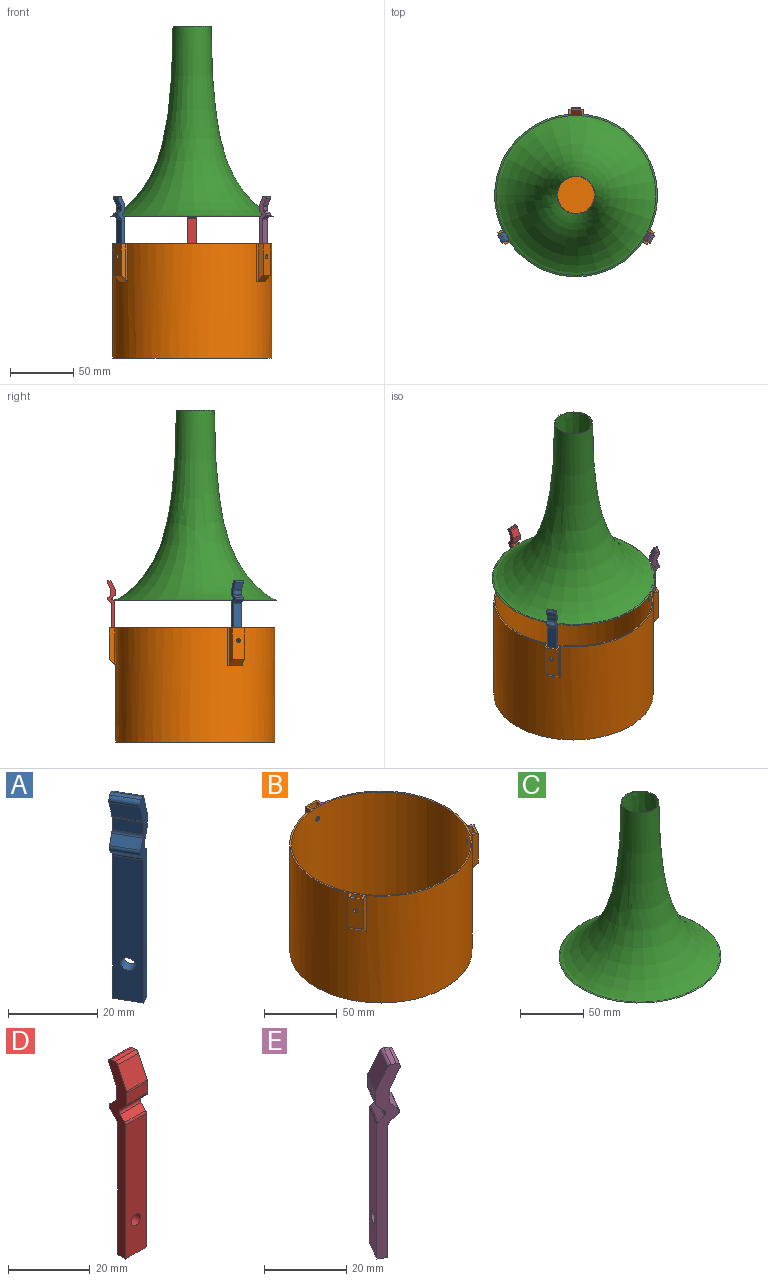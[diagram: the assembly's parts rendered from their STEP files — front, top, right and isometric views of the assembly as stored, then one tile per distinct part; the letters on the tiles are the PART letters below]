
ASSEMBLY  parts=5 mates=4
PART A: 25 faces, bbox 9.1x9.4x57.3 mm
  f0: plane 7.24x5.33mm, normal (-0.61,-0.35,0.71), area 20.4mm2, adj f12,f13,f15,f22
  f1: plane 6.24x3.6mm, normal (-0.87,-0.5,0), area 24.2mm2, adj f12,f13,f15,f16
  f2: plane 7.55x5.87mm, normal (-0.78,-0.45,-0.42), area 44.7mm2, adj f12,f13,f16,f23
  f3: plane 6.88x4.72mm, normal (0,0,1), area 9.3mm2, adj f12,f13,f23,f24
  f4: plane 7.74x6.47mm, normal (0.78,0.45,0.42), area 51.4mm2, adj f12,f13,f17,f24
  f5: plane 6.24x3.6mm, normal (0.87,0.5,0), area 24.2mm2, adj f12,f13,f17,f18
  f6: plane 7.24x5.33mm, normal (0.61,0.35,-0.71), area 20.4mm2, adj f12,f13,f18,f19
  f7: plane 7.04x4.99mm, normal (0.61,0.35,0.71), area 16.3mm2, adj f12,f13,f19,f20
  f8: plane 39.99x6.24mm, normal (0.87,0.5,0), area 278.8mm2, adj f9,f12,f13,f14,f20
  f9: plane 7.59x5.94mm, normal (0,0,-1), area 19.4mm2, adj f8,f10,f12,f13
  f10: plane 39.19x6.24mm, normal (-0.87,-0.5,0), area 273.1mm2, adj f9,f12,f13,f14,f21
  f11: plane 7.44x5.68mm, normal (-0.61,-0.35,-0.71), area 24.4mm2, adj f12,f13,f21,f22
  f12: plane 57.25x5.47mm, normal (-0.5,0.87,0), area 167.7mm2, adj f0,f1,f2,f3,f4,f5,f6,f7
  f13: plane 57.25x5.47mm, normal (0.5,-0.87,0), area 167.7mm2, adj f0,f1,f2,f3,f4,f5,f6,f7
  f14: cylinder r=1.7mm len=4.29mm, axis (-0.87,-0.5,0), area 28.8mm2, adj f8,f10
  f15: cylinder r=1mm len=6.38mm, axis (-0.5,0.87,0), area 5.7mm2, adj f0,f1,f12,f13
  f16: cylinder r=1mm len=6.28mm, axis (0.5,-0.87,0), area 3.1mm2, adj f1,f2,f12,f13
  f17: cylinder r=1mm len=6.28mm, axis (-0.5,0.87,0), area 3.1mm2, adj f4,f5,f12,f13
  f18: cylinder r=1mm len=6.38mm, axis (0.5,-0.87,0), area 5.7mm2, adj f5,f6,f12,f13
  f19: cylinder r=1mm len=6.38mm, axis (-0.5,0.87,0), area 11.3mm2, adj f6,f7,f12,f13
  f20: cylinder r=1mm len=6.38mm, axis (0.5,-0.87,0), area 5.7mm2, adj f7,f8,f12,f13
  f21: cylinder r=1mm len=6.38mm, axis (-0.5,0.87,0), area 5.7mm2, adj f10,f11,f12,f13
  f22: cylinder r=1mm len=6.38mm, axis (0.5,-0.87,0), area 11.3mm2, adj f0,f11,f12,f13
  f23: cylinder r=1mm len=6.74mm, axis (0.5,-0.87,0), area 14.5mm2, adj f2,f3,f12,f13
  f24: cylinder r=1mm len=6.69mm, axis (0.5,-0.87,0), area 8.2mm2, adj f3,f4,f12,f13
PART B: 47 faces, bbox 125.6x130.7x90 mm
  f0: cylinder r=61.6mm len=123.2mm, axis (0,0,-1), area 34497.3mm2, adj f1,f4,f16,f30,f44
  f1: plane 130.7x125.6mm, normal (0,0,1), area 560.2mm2, adj f0,f2,f5,f6,f7,f10,f11,f12
  f2: cylinder r=62.8mm len=125.6mm, axis (0,0,-1), area 34341.1mm2, adj f1,f3,f14,f17,f18,f28,f31,f32
  f3: plane 125.6x125.6mm, normal (0,0,-1), area 12389.9mm2, adj f2
  f4: plane 123.2x123.2mm, normal (0,0,1), area 11921mm2, adj f0
  f5: plane 29.11x4.45mm, normal (-1,0,0), area 119.5mm2, adj f1,f7,f8,f14,f18
  f6: plane 29.11x4.45mm, normal (1,0,0), area 119.5mm2, adj f1,f7,f8,f14,f17
  f7: plane 25x11.2mm, normal (0,1,0), area 270.9mm2, adj f1,f5,f6,f8,f15
  f8: plane 11.2x0.33mm, normal (0,0,-1), area 2mm2, adj f5,f6,f7,f14
  f9: plane 8x3.5mm, normal (0,0,1), area 28mm2, adj f10,f11,f12,f13
  f10: plane 24x8mm, normal (0,1,0), area 182.9mm2, adj f1,f9,f11,f12,f16
  f11: plane 24x3.5mm, normal (1,0,0), area 84mm2, adj f1,f9,f10,f13
  f12: plane 24x3.5mm, normal (-1,0,0), area 84mm2, adj f1,f9,f10,f13
  f13: plane 24x8mm, normal (0,-1,0), area 182.9mm2, adj f1,f9,f11,f12,f15
  f14: cone r=67.8mm half-angle=45deg, axis (0,0,1), area 79.8mm2, adj f2,f5,f6,f8,f17,f18
  f15: cylinder r=1.7mm len=3.4mm, axis (0,1,0), area 17.1mm2, adj f7,f13
  f16: cylinder r=1.7mm len=3.4mm, axis (0,1,0), area 12.8mm2, adj f0,f10
  f17: cylinder r=1mm len=30mm, axis (0,0,-1), area 43.5mm2, adj f1,f2,f6,f14
  f18: cylinder r=1mm len=30mm, axis (0,0,-1), area 43.5mm2, adj f1,f2,f5,f14
  f19: plane 29.11x3.86mm, normal (0.5,-0.87,0), area 119.5mm2, adj f1,f21,f22,f28,f32
  f20: plane 29.11x3.86mm, normal (-0.5,0.87,0), area 119.5mm2, adj f1,f21,f22,f28,f31
  f21: plane 25x9.7mm, normal (-0.87,-0.5,0), area 270.9mm2, adj f1,f19,f20,f22,f29
  f22: plane 9.87x5.89mm, normal (0,0,-1), area 2mm2, adj f19,f20,f21,f28
  f23: plane 8.68x7.03mm, normal (0,0,1), area 28mm2, adj f24,f25,f26,f27
  f24: plane 24x6.93mm, normal (-0.87,-0.5,0), area 182.9mm2, adj f1,f23,f25,f26,f30
  f25: plane 24x3.03mm, normal (-0.5,0.87,0), area 84mm2, adj f1,f23,f24,f27
  f26: plane 24x3.03mm, normal (0.5,-0.87,0), area 84mm2, adj f1,f23,f24,f27
  f27: plane 24x6.93mm, normal (0.87,0.5,0), area 182.9mm2, adj f1,f23,f25,f26,f29
  f28: cone r=67.8mm half-angle=45deg, axis (0,0,1), area 79.8mm2, adj f2,f19,f20,f22,f31,f32
  f29: cylinder r=1.7mm len=3.74mm, axis (-0.87,-0.5,0), area 17.1mm2, adj f21,f27
  f30: cylinder r=1.7mm len=3.56mm, axis (-0.87,-0.5,0), area 13.1mm2, adj f0,f24
  f31: cylinder r=1mm len=30mm, axis (0,0,-1), area 43.5mm2, adj f1,f2,f20,f28
  f32: cylinder r=1mm len=30mm, axis (0,0,-1), area 43.5mm2, adj f1,f2,f19,f28
  f33: plane 29.11x3.86mm, normal (0.5,0.87,0), area 119.5mm2, adj f1,f35,f36,f42,f46
  f34: plane 29.11x3.86mm, normal (-0.5,-0.87,0), area 119.5mm2, adj f1,f35,f36,f42,f45
  f35: plane 25x9.7mm, normal (0.87,-0.5,0), area 270.9mm2, adj f1,f33,f34,f36,f43
  f36: plane 9.87x5.89mm, normal (0,0,-1), area 2mm2, adj f33,f34,f35,f42
  f37: plane 8.68x7.03mm, normal (0,0,1), area 28mm2, adj f38,f39,f40,f41
  f38: plane 24x6.93mm, normal (0.87,-0.5,0), area 182.9mm2, adj f1,f37,f39,f40,f44
  f39: plane 24x3.03mm, normal (-0.5,-0.87,0), area 84mm2, adj f1,f37,f38,f41
  f40: plane 24x3.03mm, normal (0.5,0.87,0), area 84mm2, adj f1,f37,f38,f41
  f41: plane 24x6.93mm, normal (-0.87,0.5,0), area 182.9mm2, adj f1,f37,f39,f40,f43
  f42: cone r=67.8mm half-angle=45deg, axis (0,0,1), area 79.8mm2, adj f2,f33,f34,f36,f45,f46
  f43: cylinder r=1.7mm len=3.74mm, axis (0.87,-0.5,0), area 17.1mm2, adj f35,f41
  f44: cylinder r=1.7mm len=3.56mm, axis (0.87,-0.5,0), area 13.1mm2, adj f0,f38
  f45: cylinder r=1mm len=30mm, axis (0,0,-1), area 43.5mm2, adj f1,f2,f34,f42
  f46: cylinder r=1mm len=30mm, axis (0,0,-1), area 43.5mm2, adj f1,f2,f33,f42
PART C: 4 faces, bbox 128.5x128.5x150 mm
  f0: cone r=14.6mm half-angle=87.2deg, axis (0,0,1), area 37.2mm2, adj f1,f3
  f1: revolved ~149.98x125.94mm, area 27616.5mm2, adj f0,f2
  f2: plane 128.5x128.5mm, normal (0,0,-1), area 512.1mm2, adj f1,f3
  f3: revolved ~150x128.5mm, area 28357mm2, adj f0,f2
PART D: 25 faces, bbox 7.2x6.3x57.3 mm
  f0: plane 7.2x2mm, normal (0,0.71,0.71), area 20.4mm2, adj f12,f13,f15,f22
  f1: plane 7.2x3.36mm, normal (0,1,0), area 24.2mm2, adj f12,f13,f15,f16
  f2: plane 7.2x5.63mm, normal (0,0.91,-0.42), area 44.7mm2, adj f12,f13,f16,f23
  f3: plane 7.2x1.29mm, normal (0,0,1), area 9.3mm2, adj f12,f13,f23,f24
  f4: plane 7.2x6.47mm, normal (0,-0.91,0.42), area 51.4mm2, adj f12,f13,f17,f24
  f5: plane 7.2x3.36mm, normal (0,-1,0), area 24.2mm2, adj f12,f13,f17,f18
  f6: plane 7.2x2mm, normal (0,-0.71,-0.71), area 20.4mm2, adj f12,f13,f18,f19
  f7: plane 7.2x1.6mm, normal (0,-0.71,0.71), area 16.3mm2, adj f12,f13,f19,f20
  f8: plane 39.99x7.2mm, normal (0,-1,0), area 278.8mm2, adj f9,f12,f13,f14,f20
  f9: plane 7.2x2.7mm, normal (0,0,-1), area 19.4mm2, adj f8,f10,f12,f13
  f10: plane 39.19x7.2mm, normal (0,1,0), area 273.1mm2, adj f9,f12,f13,f14,f21
  f11: plane 7.2x2.4mm, normal (0,0.71,-0.71), area 24.4mm2, adj f12,f13,f21,f22
  f12: plane 57.25x6.31mm, normal (1,0,0), area 167.7mm2, adj f0,f1,f2,f3,f4,f5,f6,f7
  f13: plane 57.25x6.31mm, normal (-1,0,0), area 167.7mm2, adj f0,f1,f2,f3,f4,f5,f6,f7
  f14: cylinder r=1.7mm len=3.4mm, axis (0,1,0), area 28.8mm2, adj f8,f10
  f15: cylinder r=1mm len=7.2mm, axis (1,0,0), area 5.7mm2, adj f0,f1,f12,f13
  f16: cylinder r=1mm len=7.2mm, axis (-1,0,0), area 3.1mm2, adj f1,f2,f12,f13
  f17: cylinder r=1mm len=7.2mm, axis (1,0,0), area 3.1mm2, adj f4,f5,f12,f13
  f18: cylinder r=1mm len=7.2mm, axis (-1,0,0), area 5.7mm2, adj f5,f6,f12,f13
  f19: cylinder r=1mm len=7.2mm, axis (1,0,0), area 11.3mm2, adj f6,f7,f12,f13
  f20: cylinder r=1mm len=7.2mm, axis (-1,0,0), area 5.7mm2, adj f7,f8,f12,f13
  f21: cylinder r=1mm len=7.2mm, axis (1,0,0), area 5.7mm2, adj f10,f11,f12,f13
  f22: cylinder r=1mm len=7.2mm, axis (-1,0,0), area 11.3mm2, adj f0,f11,f12,f13
  f23: cylinder r=1mm len=7.2mm, axis (-1,0,0), area 14.5mm2, adj f2,f3,f12,f13
  f24: cylinder r=1mm len=7.2mm, axis (-1,0,0), area 8.2mm2, adj f3,f4,f12,f13
PART E: 25 faces, bbox 9.1x9.4x57.3 mm
  f0: plane 7.24x5.33mm, normal (0.61,-0.35,0.71), area 20.4mm2, adj f12,f13,f15,f22
  f1: plane 6.24x3.6mm, normal (0.87,-0.5,0), area 24.2mm2, adj f12,f13,f15,f16
  f2: plane 7.55x5.87mm, normal (0.78,-0.45,-0.42), area 44.7mm2, adj f12,f13,f16,f23
  f3: plane 6.88x4.72mm, normal (0,0,1), area 9.3mm2, adj f12,f13,f23,f24
  f4: plane 7.74x6.47mm, normal (-0.78,0.45,0.42), area 51.4mm2, adj f12,f13,f17,f24
  f5: plane 6.24x3.6mm, normal (-0.87,0.5,0), area 24.2mm2, adj f12,f13,f17,f18
  f6: plane 7.24x5.33mm, normal (-0.61,0.35,-0.71), area 20.4mm2, adj f12,f13,f18,f19
  f7: plane 7.04x4.99mm, normal (-0.61,0.35,0.71), area 16.3mm2, adj f12,f13,f19,f20
  f8: plane 39.99x6.24mm, normal (-0.87,0.5,0), area 278.8mm2, adj f9,f12,f13,f14,f20
  f9: plane 7.59x5.94mm, normal (0,0,-1), area 19.4mm2, adj f8,f10,f12,f13
  f10: plane 39.19x6.24mm, normal (0.87,-0.5,0), area 273.1mm2, adj f9,f12,f13,f14,f21
  f11: plane 7.44x5.68mm, normal (0.61,-0.35,-0.71), area 24.4mm2, adj f12,f13,f21,f22
  f12: plane 57.25x5.47mm, normal (-0.5,-0.87,0), area 167.7mm2, adj f0,f1,f2,f3,f4,f5,f6,f7
  f13: plane 57.25x5.47mm, normal (0.5,0.87,0), area 167.7mm2, adj f0,f1,f2,f3,f4,f5,f6,f7
  f14: cylinder r=1.7mm len=4.29mm, axis (0.87,-0.5,0), area 28.8mm2, adj f8,f10
  f15: cylinder r=1mm len=6.38mm, axis (-0.5,-0.87,0), area 5.7mm2, adj f0,f1,f12,f13
  f16: cylinder r=1mm len=6.28mm, axis (0.5,0.87,0), area 3.1mm2, adj f1,f2,f12,f13
  f17: cylinder r=1mm len=6.28mm, axis (-0.5,-0.87,0), area 3.1mm2, adj f4,f5,f12,f13
  f18: cylinder r=1mm len=6.38mm, axis (0.5,0.87,0), area 5.7mm2, adj f5,f6,f12,f13
  f19: cylinder r=1mm len=6.38mm, axis (-0.5,-0.87,0), area 11.3mm2, adj f6,f7,f12,f13
  f20: cylinder r=1mm len=6.38mm, axis (0.5,0.87,0), area 5.7mm2, adj f7,f8,f12,f13
  f21: cylinder r=1mm len=6.38mm, axis (-0.5,-0.87,0), area 5.7mm2, adj f10,f11,f12,f13
  f22: cylinder r=1mm len=6.38mm, axis (0.5,0.87,0), area 11.3mm2, adj f0,f11,f12,f13
  f23: cylinder r=1mm len=6.74mm, axis (0.5,0.87,0), area 14.5mm2, adj f2,f3,f12,f13
  f24: cylinder r=1mm len=6.69mm, axis (0.5,0.87,0), area 8.2mm2, adj f3,f4,f12,f13
PLACE A t=(-1.14,-87.27,0)mm
PLACE B t=(-0.79,-87.07,0)mm
PLACE C t=(-0.79,-87.07,111.83)mm
PLACE D t=(-0.79,-86.67,0)mm
PLACE E t=(-0.45,-87.27,0)mm
MATE slider C.f0 <-> B.f0  axis (0,0,-1) through (-0.79,-87.07,111.83)mm
MATE fastened D.f14 <-> B.f15  axis (0,1,0) through (-0.79,-20.77,80)mm
MATE fastened A.f14 <-> B.f29  axis (-0.87,-0.5,0) through (-58.21,-120.22,80)mm
MATE fastened E.f14 <-> B.f43  axis (0.87,-0.5,0) through (56.62,-120.22,80)mm
